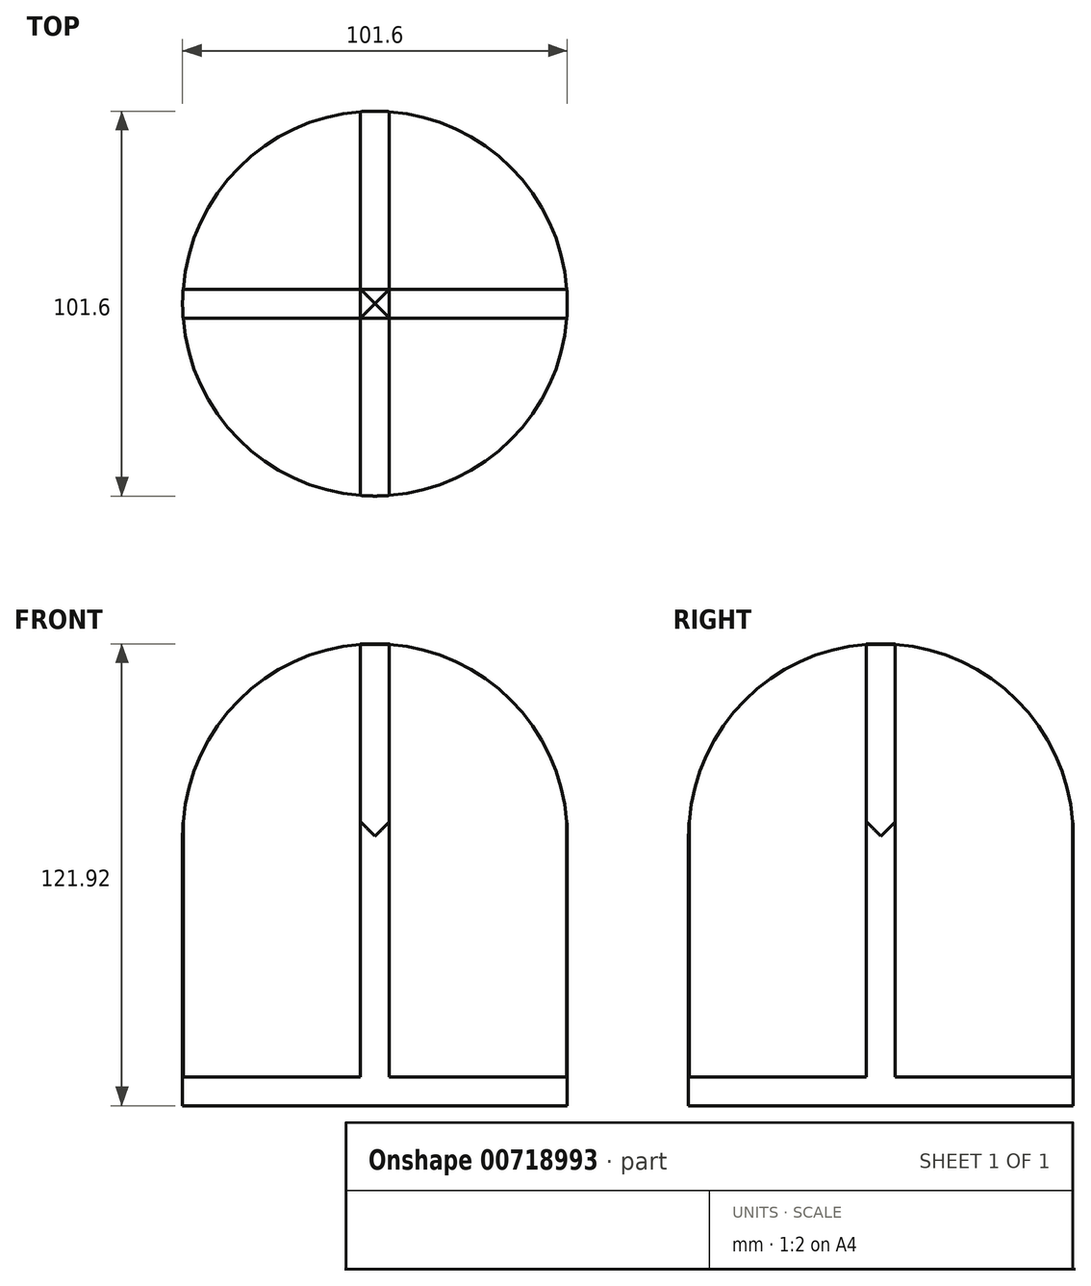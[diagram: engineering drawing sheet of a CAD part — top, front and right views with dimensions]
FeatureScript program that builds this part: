
annotation { "Feature Type Name" : "Feature", "Feature Type Description" : "" }
export const myFeature = defineFeature(function(context is Context, id is Id, definition is map)
    precondition{}
    {
        {
            var Q0;
            Q0=qCreatedBy(makeId("Top.planeOp"),FACE);
            var sketch = newSketch(context, id + "F0", { "sketchPlane" : qUnion([Q0])});
            skCircle(sketch, "E0", {"center": v(0, 0) * mm, "radius": 50.8 * mm});
            skSolve(sketch);
        }
        {
            var Q0;
            Q0 = qSketchRegion(id + "F0", true);
            extrude(context, id + "F1", {"entities" : qUnion([Q0]), "depth" : 7.62 * mm, "offsetDistance" : 25.4 * mm});
        }
        {
            var Q0;
            Q0=qCreatedBy(makeId("Front.planeOp"),FACE);
            var sketch = newSketch(context, id + "F2", { "sketchPlane" : qUnion([Q0])});
            skArc(sketch, "E1", {"start": v(50.8, 71.12) * mm, "mid": v(0, 121.92) * mm, "end": v(-50.8, 71.12) * mm});
            skLineSegment(sketch, "E2", {"start": v(-50.8, 71.12) * mm, "end": v(-50.8, 7.62) * mm});
            skLineSegment(sketch, "E3", {"start": v(-50.8, 7.62) * mm, "end": v(50.8, 7.62) * mm});
            skLineSegment(sketch, "E4", {"start": v(50.8, 7.62) * mm, "end": v(50.8, 71.12) * mm});
            skSolve(sketch);
        }
        {
            var Q0;
            Q0 = qSketchRegion(id + "F2", true);
            extrude(context, id + "F3", {"entities" : qUnion([Q0]), "operationType" : NewBodyOperationType.ADD, "depth" : 3.8 * mm, "offsetDistance" : 25.4 * mm, "hasSecondDirection" : true, "secondDirectionOppositeDirection" : true, "secondDirectionDepth" : 3.8 * mm});
        }
        {
            var Q0;
            Q0=qCreatedBy(makeId("Right.planeOp"),FACE);
            var sketch = newSketch(context, id + "F4", { "sketchPlane" : qUnion([Q0])});
            skArc(sketch, "E5", {"start": v(50.8, 71.12) * mm, "mid": v(0, 121.92) * mm, "end": v(-50.8, 71.12) * mm});
            skLineSegment(sketch, "E6", {"start": v(50.8, 71.12) * mm, "end": v(50.8, 7.62) * mm});
            skLineSegment(sketch, "E7", {"start": v(50.8, 7.62) * mm, "end": v(-50.8, 7.62) * mm});
            skLineSegment(sketch, "E8", {"start": v(-50.8, 7.62) * mm, "end": v(-50.8, 71.12) * mm});
            skSolve(sketch);
        }
        {
            var Q0;
            Q0 = qSketchRegion(id + "F4", true);
            extrude(context, id + "F5", {"entities" : qUnion([Q0]), "operationType" : NewBodyOperationType.ADD, "depth" : 3.8 * mm, "offsetDistance" : 25.4 * mm, "hasSecondDirection" : true, "secondDirectionOppositeDirection" : true, "secondDirectionDepth" : 3.8 * mm});
        }
        {
            var Q0;
            Q0=makeQuery(id+"F1.opExtrude","CAP_FACE",FACE,{"disambiguationData":[OSD([sQuery(id+"F0.wireOp",EDGE,"E0")])],"isStart":true});
            var sketch = newSketch(context, id + "F6", { "sketchPlane" : qUnion([Q0])});
            skCircle(sketch, "E9", {"center": v(0, 0) * mm, "radius": 73.85 * mm});
            skCircle(sketch, "E10", {"center": v(0, 0) * mm, "radius": 50.8 * mm});
            skSolve(sketch);
        }
        {
            var Q0;
            Q0 = qSketchRegion(id + "F6", true);
            extrude(context, id + "F7", {"entities" : qUnion([Q0]), "operationType" : NewBodyOperationType.REMOVE, "oppositeDirection" : true, "depth" : 127 * mm, "offsetDistance" : 25.4 * mm});
        }
    });
